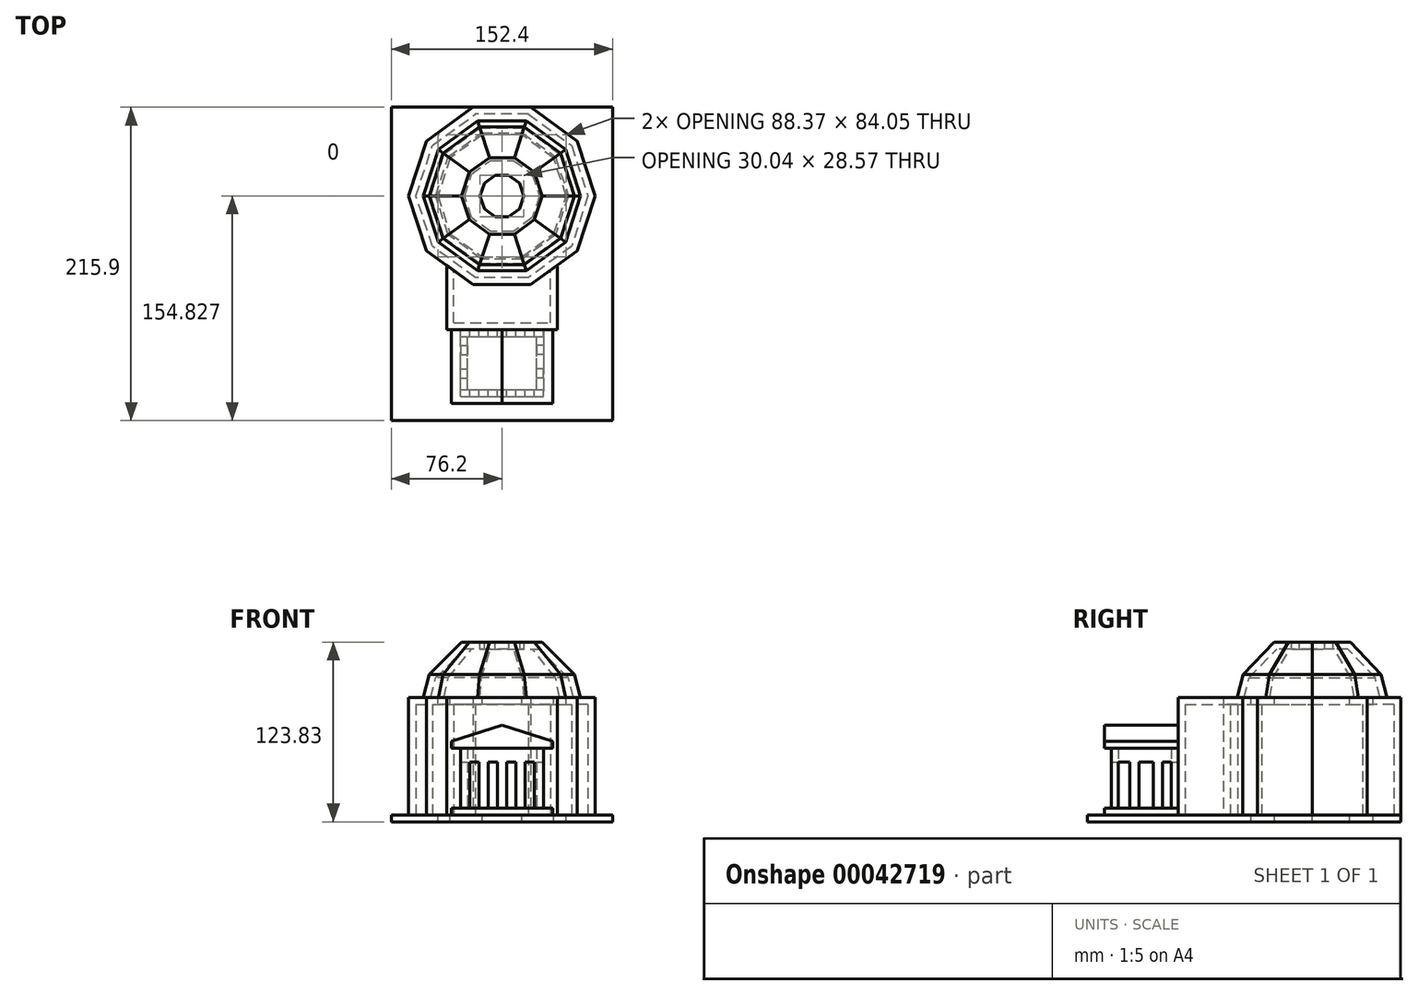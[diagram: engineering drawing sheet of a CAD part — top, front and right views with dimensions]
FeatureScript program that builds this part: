
annotation { "Feature Type Name" : "Feature", "Feature Type Description" : "" }
export const myFeature = defineFeature(function(context is Context, id is Id, definition is map)
    precondition{}
    {
        {
            var Q0;
            Q0=qCreatedBy(makeId("Top.planeOp"),FACE);
            var sketch = newSketch(context, id + "F0", { "sketchPlane" : qUnion([Q0])});
            skLineSegment(sketch, "E0.rect.bottom", {"start": v(76.2, 107.95) * mm, "end": v(-76.2, 107.95) * mm});
            skLineSegment(sketch, "E0.rect.top", {"start": v(76.2, -107.95) * mm, "end": v(-76.2, -107.95) * mm});
            skLineSegment(sketch, "E0.rect.left", {"start": v(76.2, 107.95) * mm, "end": v(76.2, -107.95) * mm});
            skLineSegment(sketch, "E0.rect.right", {"start": v(-76.2, 107.95) * mm, "end": v(-76.2, -107.95) * mm});
            skPoint(sketch, "E0.rect.middle", {"position": v(0, 0) * mm});
            skSolve(sketch);
        }
        {
            var Q0;
            Q0 = qSketchRegion(id + "F0", true);
            extrude(context, id + "F1", {"entities" : qUnion([Q0]), "depth" : 4.76 * mm});
        }
        {
            var Q0;
            Q0=makeQuery(id+"F1.opExtrude","CAP_FACE",FACE,{"disambiguationData":[OSD([sQuery(id+"F0.wireOp",EDGE,"E0.rect.bottom"),sQuery(id+"F0.wireOp",EDGE,"E0.rect.top"),sQuery(id+"F0.wireOp",EDGE,"E0.rect.left"),sQuery(id+"F0.wireOp",EDGE,"E0.rect.right")])],"isStart":false});
            var sketch = newSketch(context, id + "F2", { "sketchPlane" : qUnion([Q0])});
            skLineSegment(sketch, "E1.bottom", {"start": v(-34.93, -96.19) * mm, "end": v(34.92, -96.19) * mm});
            skLineSegment(sketch, "E1.top", {"start": v(-34.93, -45.39) * mm, "end": v(34.92, -45.39) * mm});
            skLineSegment(sketch, "E1.left", {"start": v(-34.93, -96.19) * mm, "end": v(-34.93, -45.39) * mm});
            skLineSegment(sketch, "E1.right", {"start": v(34.92, -96.19) * mm, "end": v(34.92, -45.39) * mm});
            skSolve(sketch);
        }
        {
            var Q0;
            Q0 = qSketchRegion(id + "F2", true);
            extrude(context, id + "F3", {"entities" : qUnion([Q0]), "depth" : 4.76 * mm});
        }
        {
            var Q0;
            Q0=makeQuery(id+"F3.opExtrude","CAP_FACE",FACE,{"disambiguationData":[OSD([sQuery(id+"F2.wireOp",EDGE,"E1.bottom"),sQuery(id+"F2.wireOp",EDGE,"E1.top"),sQuery(id+"F2.wireOp",EDGE,"E1.left"),sQuery(id+"F2.wireOp",EDGE,"E1.right")])],"isStart":false});
            var sketch = newSketch(context, id + "F4", { "sketchPlane" : qUnion([Q0])});
            skLineSegment(sketch, "E2.bottom", {"start": v(-28.58, -91.43) * mm, "end": v(-22.23, -91.43) * mm});
            skLineSegment(sketch, "E2.top", {"start": v(-28.58, -86.66) * mm, "end": v(-22.22, -86.66) * mm});
            skLineSegment(sketch, "E2.left", {"start": v(-28.58, -91.43) * mm, "end": v(-28.58, -86.66) * mm});
            skLineSegment(sketch, "E2.right", {"start": v(-22.22, -91.43) * mm, "end": v(-22.22, -86.66) * mm});
            skLineSegment(sketch, "E3.1.0.0", {"start": v(-15.88, -86.66) * mm, "end": v(-9.52, -86.66) * mm});
            skLineSegment(sketch, "E3.1.0.1", {"start": v(-15.88, -91.43) * mm, "end": v(-15.88, -86.66) * mm});
            skLineSegment(sketch, "E3.1.0.2", {"start": v(-15.88, -91.43) * mm, "end": v(-9.53, -91.43) * mm});
            skLineSegment(sketch, "E3.1.0.3", {"start": v(-9.52, -91.43) * mm, "end": v(-9.52, -86.66) * mm});
            skLineSegment(sketch, "E3.2.0.0", {"start": v(-3.18, -86.66) * mm, "end": v(3.18, -86.66) * mm});
            skLineSegment(sketch, "E3.2.0.1", {"start": v(-3.17, -91.43) * mm, "end": v(-3.17, -86.66) * mm});
            skLineSegment(sketch, "E3.2.0.2", {"start": v(-3.18, -91.43) * mm, "end": v(3.18, -91.43) * mm});
            skLineSegment(sketch, "E3.2.0.3", {"start": v(3.18, -91.43) * mm, "end": v(3.18, -86.66) * mm});
            skLineSegment(sketch, "E3.3.0.0", {"start": v(9.52, -86.66) * mm, "end": v(15.88, -86.66) * mm});
            skLineSegment(sketch, "E3.3.0.1", {"start": v(9.53, -91.43) * mm, "end": v(9.53, -86.66) * mm});
            skLineSegment(sketch, "E3.3.0.2", {"start": v(9.52, -91.43) * mm, "end": v(15.88, -91.43) * mm});
            skLineSegment(sketch, "E3.3.0.3", {"start": v(15.88, -91.43) * mm, "end": v(15.88, -86.66) * mm});
            skLineSegment(sketch, "E3.direction1", {"start": v(-28.58, -86.66) * mm, "end": v(-15.88, -86.66) * mm, "construction": true});
            skLineSegment(sketch, "E4.0.4.0", {"start": v(22.23, -86.66) * mm, "end": v(28.58, -86.66) * mm});
            skLineSegment(sketch, "E4.3.4.0", {"start": v(22.23, -91.43) * mm, "end": v(22.23, -86.66) * mm});
            skLineSegment(sketch, "E4.6.4.0", {"start": v(22.23, -91.43) * mm, "end": v(28.58, -91.43) * mm});
            skLineSegment(sketch, "E4.9.4.0", {"start": v(28.58, -91.43) * mm, "end": v(28.58, -86.66) * mm});
            skLineSegment(sketch, "E5.bottom", {"start": v(-28.58, -50.15) * mm, "end": v(-22.23, -50.15) * mm});
            skLineSegment(sketch, "E6.3.0.0", {"start": v(9.52, -45.39) * mm, "end": v(15.87, -45.39) * mm});
            skLineSegment(sketch, "E6.3.0.2", {"start": v(9.52, -50.15) * mm, "end": v(15.87, -50.15) * mm});
            skLineSegment(sketch, "E7.6.4.0", {"start": v(22.22, -50.15) * mm, "end": v(28.57, -50.15) * mm});
            skLineSegment(sketch, "E5.top", {"start": v(-28.58, -45.39) * mm, "end": v(-22.23, -45.39) * mm});
            skLineSegment(sketch, "E6.3.0.1", {"start": v(9.52, -50.15) * mm, "end": v(9.52, -45.39) * mm});
            skLineSegment(sketch, "E5.left", {"start": v(-28.58, -50.15) * mm, "end": v(-28.58, -45.39) * mm});
            skLineSegment(sketch, "E5.right", {"start": v(-22.23, -50.15) * mm, "end": v(-22.23, -45.39) * mm});
            skLineSegment(sketch, "E6.1.0.0", {"start": v(-15.88, -45.39) * mm, "end": v(-9.53, -45.39) * mm});
            skLineSegment(sketch, "E6.3.0.3", {"start": v(15.87, -50.15) * mm, "end": v(15.87, -45.39) * mm});
            skLineSegment(sketch, "E6.direction1", {"start": v(-28.58, -45.39) * mm, "end": v(-15.88, -45.39) * mm, "construction": true});
            skLineSegment(sketch, "E7.9.4.0", {"start": v(28.57, -50.15) * mm, "end": v(28.57, -45.39) * mm});
            skLineSegment(sketch, "E7.3.4.0", {"start": v(22.22, -50.15) * mm, "end": v(22.22, -45.39) * mm});
            skLineSegment(sketch, "E6.2.0.3", {"start": v(3.17, -50.15) * mm, "end": v(3.17, -45.39) * mm});
            skLineSegment(sketch, "E6.2.0.2", {"start": v(-3.18, -50.15) * mm, "end": v(3.17, -50.15) * mm});
            skLineSegment(sketch, "E7.0.4.0", {"start": v(22.22, -45.39) * mm, "end": v(28.57, -45.39) * mm});
            skLineSegment(sketch, "E6.2.0.1", {"start": v(-3.18, -50.15) * mm, "end": v(-3.18, -45.39) * mm});
            skLineSegment(sketch, "E6.2.0.0", {"start": v(-3.18, -45.39) * mm, "end": v(3.17, -45.39) * mm});
            skLineSegment(sketch, "E6.1.0.3", {"start": v(-9.53, -50.15) * mm, "end": v(-9.53, -45.39) * mm});
            skLineSegment(sketch, "E6.1.0.2", {"start": v(-15.88, -50.15) * mm, "end": v(-9.53, -50.15) * mm});
            skLineSegment(sketch, "E6.1.0.1", {"start": v(-15.88, -50.15) * mm, "end": v(-15.88, -45.39) * mm});
            skLineSegment(sketch, "E8", {"start": v(28.58, -67.47) * mm, "end": v(-34.93, -67.47) * mm, "construction": true});
            skLineSegment(sketch, "E9.bottom", {"start": v(28.57, -78.73) * mm, "end": v(23.81, -78.73) * mm});
            skLineSegment(sketch, "E9.top", {"start": v(28.58, -72.38) * mm, "end": v(23.81, -72.38) * mm});
            skLineSegment(sketch, "E9.left", {"start": v(28.58, -78.73) * mm, "end": v(28.58, -72.38) * mm});
            skLineSegment(sketch, "E9.right", {"start": v(23.81, -78.73) * mm, "end": v(23.81, -72.38) * mm});
            skLineSegment(sketch, "E10.MirrorCS", {"start": v(28.58, -62.56) * mm, "end": v(23.81, -62.56) * mm});
            skLineSegment(sketch, "E11.MirrorCS", {"start": v(23.81, -56.21) * mm, "end": v(23.81, -62.56) * mm});
            skLineSegment(sketch, "E12.MirrorCS", {"start": v(28.58, -56.21) * mm, "end": v(28.58, -62.56) * mm});
            skLineSegment(sketch, "E13.MirrorCS", {"start": v(28.57, -56.21) * mm, "end": v(23.81, -56.21) * mm});
            skLineSegment(sketch, "E14", {"start": v(0, -96.19) * mm, "end": v(0, -45.39) * mm, "construction": true});
            skLineSegment(sketch, "E15.MirrorCS", {"start": v(-28.58, -56.21) * mm, "end": v(-23.81, -56.21) * mm});
            skLineSegment(sketch, "E16.MirrorCS", {"start": v(-28.58, -56.21) * mm, "end": v(-28.58, -62.56) * mm});
            skLineSegment(sketch, "E17.MirrorCS", {"start": v(-28.58, -72.38) * mm, "end": v(-23.81, -72.38) * mm});
            skLineSegment(sketch, "E18.MirrorCS", {"start": v(-28.58, -62.56) * mm, "end": v(-23.81, -62.56) * mm});
            skLineSegment(sketch, "E19.MirrorCS", {"start": v(-28.58, -78.73) * mm, "end": v(-23.81, -78.73) * mm});
            skLineSegment(sketch, "E20.MirrorCS", {"start": v(-23.81, -56.21) * mm, "end": v(-23.81, -62.56) * mm});
            skLineSegment(sketch, "E21.MirrorCS", {"start": v(-28.58, -78.73) * mm, "end": v(-28.58, -72.38) * mm});
            skLineSegment(sketch, "E22.MirrorCS", {"start": v(-23.81, -78.73) * mm, "end": v(-23.81, -72.38) * mm});
            skSolve(sketch);
        }
        {
            var Q0;
            Q0=makeQuery(id+"F4.imprint","IMPRINT",FACE,{"disambiguationData":[TD([[makeQuery(id+"F4.imprint","IMPRINT",EDGE,{"derivedFrom":sQuery(id+"F4.wireOp",EDGE,"E5.bottom")}),1.0]])]});
            var Q1;
            Q1=makeQuery(id+"F4.imprint","IMPRINT",FACE,{"disambiguationData":[TD([[makeQuery(id+"F4.imprint","IMPRINT",EDGE,{"derivedFrom":sQuery(id+"F4.wireOp",EDGE,"E6.1.0.0")}),-1.0]])]});
            var Q2;
            Q2=makeQuery(id+"F4.imprint","IMPRINT",FACE,{"disambiguationData":[TD([[makeQuery(id+"F4.imprint","IMPRINT",EDGE,{"derivedFrom":sQuery(id+"F4.wireOp",EDGE,"E6.2.0.3")}),1.0]])]});
            var Q3;
            Q3=makeQuery(id+"F4.imprint","IMPRINT",FACE,{"disambiguationData":[TD([[makeQuery(id+"F4.imprint","IMPRINT",EDGE,{"derivedFrom":sQuery(id+"F4.wireOp",EDGE,"E6.3.0.0")}),-1.0]])]});
            var Q4;
            Q4=makeQuery(id+"F4.imprint","IMPRINT",FACE,{"disambiguationData":[TD([[makeQuery(id+"F4.imprint","IMPRINT",EDGE,{"derivedFrom":sQuery(id+"F4.wireOp",EDGE,"E7.6.4.0")}),1.0]])]});
            var Q5;
            Q5=makeQuery(id+"F4.imprint","IMPRINT",FACE,{"disambiguationData":[TD([[makeQuery(id+"F4.imprint","IMPRINT",EDGE,{"derivedFrom":sQuery(id+"F4.wireOp",EDGE,"E10.MirrorCS")}),-1.0]])]});
            var Q6;
            Q6=makeQuery(id+"F4.imprint","IMPRINT",FACE,{"disambiguationData":[TD([[makeQuery(id+"F4.imprint","IMPRINT",EDGE,{"derivedFrom":sQuery(id+"F4.wireOp",EDGE,"E9.bottom")}),-1.0]])]});
            var Q7;
            Q7=makeQuery(id+"F4.imprint","IMPRINT",FACE,{"disambiguationData":[TD([[makeQuery(id+"F4.imprint","IMPRINT",EDGE,{"derivedFrom":sQuery(id+"F4.wireOp",EDGE,"E4.0.4.0")}),-1.0]])]});
            var Q8;
            Q8=makeQuery(id+"F4.imprint","IMPRINT",FACE,{"disambiguationData":[TD([[makeQuery(id+"F4.imprint","IMPRINT",EDGE,{"derivedFrom":sQuery(id+"F4.wireOp",EDGE,"E3.3.0.0")}),-1.0]])]});
            var Q9;
            Q9=makeQuery(id+"F4.imprint","IMPRINT",FACE,{"disambiguationData":[TD([[makeQuery(id+"F4.imprint","IMPRINT",EDGE,{"derivedFrom":sQuery(id+"F4.wireOp",EDGE,"E3.2.0.0")}),-1.0]])]});
            var Q10;
            Q10=makeQuery(id+"F4.imprint","IMPRINT",FACE,{"disambiguationData":[TD([[makeQuery(id+"F4.imprint","IMPRINT",EDGE,{"derivedFrom":sQuery(id+"F4.wireOp",EDGE,"E3.1.0.0")}),-1.0]])]});
            var Q11;
            Q11=makeQuery(id+"F4.imprint","IMPRINT",FACE,{"disambiguationData":[TD([[makeQuery(id+"F4.imprint","IMPRINT",EDGE,{"derivedFrom":sQuery(id+"F4.wireOp",EDGE,"E2.bottom")}),1.0]])]});
            var Q12;
            Q12=makeQuery(id+"F4.imprint","IMPRINT",FACE,{"disambiguationData":[TD([[makeQuery(id+"F4.imprint","IMPRINT",EDGE,{"derivedFrom":sQuery(id+"F4.wireOp",EDGE,"E17.MirrorCS")}),-1.0]])]});
            var Q13;
            Q13=makeQuery(id+"F4.imprint","IMPRINT",FACE,{"disambiguationData":[TD([[makeQuery(id+"F4.imprint","IMPRINT",EDGE,{"derivedFrom":sQuery(id+"F4.wireOp",EDGE,"E15.MirrorCS")}),-1.0]])]});
            extrude(context, id + "F5", {"entities" : qUnion([Q0, Q1, Q2, Q3, Q4, Q5, Q6, Q7, Q8, Q9, Q10, Q11, Q12, Q13]), "operationType" : NewBodyOperationType.ADD, "depth" : 31.75 * mm});
        }
        {
            var Q0;
            Q0=makeQuery(id+"F5.opExtrude","CAP_FACE",FACE,{"disambiguationData":[OSD([sQuery(id+"F4.wireOp",EDGE,"E5.bottom"),sQuery(id+"F4.wireOp",EDGE,"E5.top"),sQuery(id+"F4.wireOp",EDGE,"E5.left"),sQuery(id+"F4.wireOp",EDGE,"E5.right")])],"isStart":false});
            var sketch = newSketch(context, id + "F6", { "sketchPlane" : qUnion([Q0])});
            skPoint(sketch, "E23.0", {"position": v(-28.58, -45.39) * mm});
            skPoint(sketch, "E24.0", {"position": v(-23.81, -56.21) * mm});
            skPoint(sketch, "E25.0", {"position": v(28.58, -91.43) * mm});
            skPoint(sketch, "E26.0", {"position": v(23.81, -78.73) * mm});
            skLineSegment(sketch, "E27.bottom", {"start": v(-28.58, -45.39) * mm, "end": v(28.58, -45.39) * mm});
            skLineSegment(sketch, "E27.top", {"start": v(-28.58, -91.43) * mm, "end": v(28.58, -91.43) * mm});
            skLineSegment(sketch, "E27.left", {"start": v(-28.58, -45.39) * mm, "end": v(-28.58, -91.43) * mm});
            skLineSegment(sketch, "E27.right", {"start": v(28.57, -45.39) * mm, "end": v(28.57, -91.43) * mm});
            skLineSegment(sketch, "E28.0", {"start": v(22.23, -86.66) * mm, "end": v(28.58, -86.66) * mm});
            skLineSegment(sketch, "E29.0", {"start": v(-28.58, -50.15) * mm, "end": v(-22.23, -50.15) * mm});
            skPoint(sketch, "E30.firstSnap0", {"position": v(25.4, -86.66) * mm});
            skLineSegment(sketch, "E30.bottom", {"start": v(23.81, -86.66) * mm, "end": v(-23.81, -86.66) * mm});
            skLineSegment(sketch, "E30.top", {"start": v(23.81, -50.15) * mm, "end": v(-23.81, -50.15) * mm});
            skLineSegment(sketch, "E30.left", {"start": v(23.81, -86.66) * mm, "end": v(23.81, -50.15) * mm});
            skLineSegment(sketch, "E30.right", {"start": v(-23.81, -86.66) * mm, "end": v(-23.81, -50.15) * mm});
            skSolve(sketch);
        }
        {
            var Q0;
            Q0 = qSketchRegion(id + "F6", true);
            extrude(context, id + "F7", {"entities" : qUnion([Q0]), "operationType" : NewBodyOperationType.ADD, "depth" : 9.52 * mm});
        }
        {
            var Q0;
            Q0=makeQuery(id+"F3.opExtrude","SWEPT_FACE",FACE,{"disambiguationData":[OSD([sQuery(id+"F2.wireOp",EDGE,"E1.bottom")])]});
            var sketch = newSketch(context, id + "F8", { "sketchPlane" : qUnion([Q0])});
            skLineSegment(sketch, "E31.0", {"start": v(-28.58, 50.8) * mm, "end": v(28.58, 50.8) * mm});
            skLineSegment(sketch, "E32", {"start": v(-34.93, 50.8) * mm, "end": v(-28.58, 50.8) * mm});
            skLineSegment(sketch, "E33", {"start": v(34.92, 50.8) * mm, "end": v(28.58, 50.8) * mm});
            skLineSegment(sketch, "E34", {"start": v(34.92, 50.8) * mm, "end": v(34.92, 55.56) * mm});
            skLineSegment(sketch, "E35", {"start": v(-34.93, 50.8) * mm, "end": v(-34.93, 55.56) * mm});
            skLineSegment(sketch, "E36", {"start": v(0, 50.8) * mm, "end": v(0, 66.67) * mm, "construction": true});
            skPoint(sketch, "E36.endSnap0", {"position": v(0, 50.8) * mm});
            skLineSegment(sketch, "E37", {"start": v(0, 66.67) * mm, "end": v(-34.93, 55.56) * mm});
            skLineSegment(sketch, "E38", {"start": v(0, 66.67) * mm, "end": v(34.92, 55.56) * mm});
            skSolve(sketch);
        }
        {
            var Q0;
            Q0 = qSketchRegion(id + "F8", true);
            var Q1;
            Q1=makeQuery(id+"F7.boolean.opBoolean","MERGE",FACE,{"derivedFrom":[makeQuery(id+"F5.boolean.opBoolean","MERGE",FACE,{"derivedFrom":[makeQuery(id+"F3.opExtrude","SWEPT_FACE",FACE,{"disambiguationData":[OSD([sQuery(id+"F2.wireOp",EDGE,"E1.top")])]}),makeQuery(id+"F5.opExtrude","SWEPT_FACE",FACE,{"disambiguationData":[OSD([sQuery(id+"F4.wireOp",EDGE,"E6.3.0.0")])]}),makeQuery(id+"F5.opExtrude","SWEPT_FACE",FACE,{"disambiguationData":[OSD([sQuery(id+"F4.wireOp",EDGE,"E5.top")])]}),makeQuery(id+"F5.opExtrude","SWEPT_FACE",FACE,{"disambiguationData":[OSD([sQuery(id+"F4.wireOp",EDGE,"E6.1.0.0")])]}),makeQuery(id+"F5.opExtrude","SWEPT_FACE",FACE,{"disambiguationData":[OSD([sQuery(id+"F4.wireOp",EDGE,"E7.0.4.0")])]}),makeQuery(id+"F5.opExtrude","SWEPT_FACE",FACE,{"disambiguationData":[OSD([sQuery(id+"F4.wireOp",EDGE,"E6.2.0.0")])]})]}),makeQuery(id+"F7.opExtrude","SWEPT_FACE",FACE,{"disambiguationData":[OSD([sQuery(id+"F6.wireOp",EDGE,"E27.bottom")])]})]});
            extrude(context, id + "F9", {"entities" : qUnion([Q0]), "operationType" : NewBodyOperationType.ADD, "endBound" : BoundingType.UP_TO_SURFACE, "oppositeDirection" : true, "endBoundEntityFace" : qUnion([Q1]), "depth" : 25.4 * mm});
        }
        {
            var Q0;
            Q0=makeQuery(id+"F1.opExtrude","CAP_FACE",FACE,{"disambiguationData":[OSD([sQuery(id+"F0.wireOp",EDGE,"E0.rect.bottom"),sQuery(id+"F0.wireOp",EDGE,"E0.rect.top"),sQuery(id+"F0.wireOp",EDGE,"E0.rect.left"),sQuery(id+"F0.wireOp",EDGE,"E0.rect.right")])],"isStart":false});
            var sketch = newSketch(context, id + "F10", { "sketchPlane" : qUnion([Q0])});
            skCircle(sketch, "E39.cCircle", {"center": v(0, 46.88) * mm, "radius": 61.07 * mm, "construction": true});
            skLineSegment(sketch, "E39.0", {"start": v(-19.84, 107.95) * mm, "end": v(19.84, 107.95) * mm});
            skLineSegment(sketch, "E39.1", {"start": v(19.84, 107.95) * mm, "end": v(51.95, 84.62) * mm});
            skLineSegment(sketch, "E39.2", {"start": v(51.95, 84.62) * mm, "end": v(64.22, 46.88) * mm});
            skLineSegment(sketch, "E39.3", {"start": v(64.22, 46.88) * mm, "end": v(51.95, 9.13) * mm});
            skLineSegment(sketch, "E39.4", {"start": v(51.95, 9.13) * mm, "end": v(19.84, -14.2) * mm});
            skLineSegment(sketch, "E39.5", {"start": v(19.84, -14.2) * mm, "end": v(-19.84, -14.2) * mm});
            skLineSegment(sketch, "E39.6", {"start": v(-19.84, -14.2) * mm, "end": v(-51.95, 9.13) * mm});
            skLineSegment(sketch, "E39.7", {"start": v(-51.95, 9.13) * mm, "end": v(-64.22, 46.88) * mm});
            skLineSegment(sketch, "E39.8", {"start": v(-64.22, 46.88) * mm, "end": v(-51.95, 84.62) * mm});
            skLineSegment(sketch, "E39.9", {"start": v(-51.95, 84.62) * mm, "end": v(-19.84, 107.95) * mm});
            skPoint(sketch, "E39.0.midPoint", {"position": v(0, 107.95) * mm});
            skSolve(sketch);
        }
        {
            var Q0;
            Q0 = qSketchRegion(id + "F10", true);
            extrude(context, id + "F11", {"entities" : qUnion([Q0]), "depth" : 80.96 * mm});
        }
        {
            var Q0;
            Q0=makeQuery(id+"F1.opExtrude","CAP_FACE",FACE,{"disambiguationData":[OSD([sQuery(id+"F0.wireOp",EDGE,"E0.rect.bottom"),sQuery(id+"F0.wireOp",EDGE,"E0.rect.top"),sQuery(id+"F0.wireOp",EDGE,"E0.rect.left"),sQuery(id+"F0.wireOp",EDGE,"E0.rect.right")])],"isStart":false});
            var sketch = newSketch(context, id + "F12", { "sketchPlane" : qUnion([Q0])});
            skLineSegment(sketch, "E40.0", {"start": v(-19.84, -14.2) * mm, "end": v(-51.95, 9.13) * mm});
            skLineSegment(sketch, "E41.0", {"start": v(19.84, -14.2) * mm, "end": v(-19.84, -14.2) * mm});
            skLineSegment(sketch, "E42.0", {"start": v(51.95, 9.13) * mm, "end": v(19.84, -14.2) * mm});
            skLineSegment(sketch, "E43.0", {"start": v(-34.93, -44.45) * mm, "end": v(34.92, -44.45) * mm});
            skLineSegment(sketch, "E44", {"start": v(-38.1, -45.39) * mm, "end": v(38.1, -45.39) * mm});
            skPoint(sketch, "E45.0", {"position": v(0, -45.39) * mm});
            skLineSegment(sketch, "E46", {"start": v(-38.1, -45.39) * mm, "end": v(-38.1, -0.93) * mm});
            skLineSegment(sketch, "E47", {"start": v(38.1, -45.39) * mm, "end": v(38.1, -0.93) * mm});
            skSolve(sketch);
        }
        {
            var Q0;
            Q0 = qSketchRegion(id + "F12", true);
            extrude(context, id + "F13", {"entities" : qUnion([Q0]), "depth" : 80.96 * mm});
        }
        {
            var Q0;
            Q0=makeQuery(id+"F11.opExtrude","CAP_FACE",FACE,{"disambiguationData":[OSD([sQuery(id+"F10.wireOp",EDGE,"E39.0"),sQuery(id+"F10.wireOp",EDGE,"E39.1"),sQuery(id+"F10.wireOp",EDGE,"E39.2"),sQuery(id+"F10.wireOp",EDGE,"E39.3"),sQuery(id+"F10.wireOp",EDGE,"E39.4"),sQuery(id+"F10.wireOp",EDGE,"E39.5"),sQuery(id+"F10.wireOp",EDGE,"E39.6"),sQuery(id+"F10.wireOp",EDGE,"E39.7"),sQuery(id+"F10.wireOp",EDGE,"E39.8"),sQuery(id+"F10.wireOp",EDGE,"E39.9")])],"isStart":true});
            shell(context, id + "F14", {"entities" : qUnion([Q0]), "thickness" : 4.76 * mm});
        }
        {
            var Q0;
            Q0=makeQuery(id+"F13.opExtrude","CAP_FACE",FACE,{"disambiguationData":[OSD([sQuery(id+"F12.wireOp",EDGE,"E40.0"),sQuery(id+"F12.wireOp",EDGE,"E41.0"),sQuery(id+"F12.wireOp",EDGE,"E42.0"),sQuery(id+"F12.wireOp",EDGE,"E44"),sQuery(id+"F12.wireOp",EDGE,"E46"),sQuery(id+"F12.wireOp",EDGE,"E47")])],"isStart":true});
            var Q1;
            Q1=makeQuery(id+"F13.opExtrude","SWEPT_FACE",FACE,{"disambiguationData":[OSD([sQuery(id+"F12.wireOp",EDGE,"E41.0")])]});
            var Q2;
            Q2=makeQuery(id+"F13.opExtrude","SWEPT_FACE",FACE,{"disambiguationData":[OSD([sQuery(id+"F12.wireOp",EDGE,"E42.0")])]});
            var Q3;
            Q3=makeQuery(id+"F13.opExtrude","SWEPT_FACE",FACE,{"disambiguationData":[OSD([sQuery(id+"F12.wireOp",EDGE,"E40.0")])]});
            shell(context, id + "F15", {"entities" : qUnion([Q0, Q1, Q2, Q3]), "thickness" : 4.76 * mm});
        }
        {
            var Q0;
            Q0=makeQuery(id+"F11.opExtrude","CAP_FACE",FACE,{"disambiguationData":[OSD([sQuery(id+"F10.wireOp",EDGE,"E39.0"),sQuery(id+"F10.wireOp",EDGE,"E39.1"),sQuery(id+"F10.wireOp",EDGE,"E39.2"),sQuery(id+"F10.wireOp",EDGE,"E39.3"),sQuery(id+"F10.wireOp",EDGE,"E39.4"),sQuery(id+"F10.wireOp",EDGE,"E39.5"),sQuery(id+"F10.wireOp",EDGE,"E39.6"),sQuery(id+"F10.wireOp",EDGE,"E39.7"),sQuery(id+"F10.wireOp",EDGE,"E39.8"),sQuery(id+"F10.wireOp",EDGE,"E39.9")])],"isStart":false});
            var sketch = newSketch(context, id + "F16", { "sketchPlane" : qUnion([Q0])});
            skLineSegment(sketch, "E48.0", {"start": v(44.19, 46.88) * mm, "end": v(35.75, 72.85) * mm});
            skLineSegment(sketch, "E48.1", {"start": v(35.75, 20.9) * mm, "end": v(44.19, 46.88) * mm});
            skLineSegment(sketch, "E48.2", {"start": v(35.75, 72.85) * mm, "end": v(13.65, 88.9) * mm});
            skLineSegment(sketch, "E48.3", {"start": v(13.65, 4.85) * mm, "end": v(35.75, 20.9) * mm});
            skLineSegment(sketch, "E48.4", {"start": v(-13.65, 4.85) * mm, "end": v(13.65, 4.85) * mm});
            skLineSegment(sketch, "E48.5", {"start": v(-35.75, 20.9) * mm, "end": v(-13.65, 4.85) * mm});
            skLineSegment(sketch, "E48.6", {"start": v(13.65, 88.9) * mm, "end": v(-13.65, 88.9) * mm});
            skLineSegment(sketch, "E48.7", {"start": v(-13.65, 88.9) * mm, "end": v(-35.75, 72.85) * mm});
            skLineSegment(sketch, "E48.8", {"start": v(-35.75, 72.85) * mm, "end": v(-44.19, 46.88) * mm});
            skLineSegment(sketch, "E48.9", {"start": v(-44.19, 46.88) * mm, "end": v(-35.75, 20.9) * mm});
            skSolve(sketch);
        }
        {
            var Q0;
            Q0=makeQuery(id+"F16.imprint","IMPRINT",FACE,{"disambiguationData":[TD([[makeQuery(id+"F16.imprint","IMPRINT",EDGE,{"derivedFrom":sQuery(id+"F16.wireOp",EDGE,"E48.0")}),1.0]])]});
            extrude(context, id + "F17", {"entities" : qUnion([Q0]), "operationType" : NewBodyOperationType.REMOVE, "endBound" : BoundingType.THROUGH_ALL, "oppositeDirection" : true, "depth" : 25.4 * mm});
        }
        {
            var Q0;
            Q0=makeQuery(id+"F11.opExtrude","CAP_FACE",FACE,{"disambiguationData":[OSD([sQuery(id+"F10.wireOp",EDGE,"E39.0"),sQuery(id+"F10.wireOp",EDGE,"E39.1"),sQuery(id+"F10.wireOp",EDGE,"E39.2"),sQuery(id+"F10.wireOp",EDGE,"E39.3"),sQuery(id+"F10.wireOp",EDGE,"E39.4"),sQuery(id+"F10.wireOp",EDGE,"E39.5"),sQuery(id+"F10.wireOp",EDGE,"E39.6"),sQuery(id+"F10.wireOp",EDGE,"E39.7"),sQuery(id+"F10.wireOp",EDGE,"E39.8"),sQuery(id+"F10.wireOp",EDGE,"E39.9")])],"isStart":false});
            var sketch = newSketch(context, id + "F18", { "sketchPlane" : qUnion([Q0])});
            skLineSegment(sketch, "E49.0", {"start": v(54.2, 46.88) * mm, "end": v(43.85, 78.74) * mm});
            skLineSegment(sketch, "E49.1", {"start": v(43.85, 15.02) * mm, "end": v(54.2, 46.88) * mm});
            skLineSegment(sketch, "E49.2", {"start": v(43.85, 78.74) * mm, "end": v(16.75, 98.43) * mm});
            skLineSegment(sketch, "E49.3", {"start": v(16.75, -4.67) * mm, "end": v(43.85, 15.02) * mm});
            skLineSegment(sketch, "E49.4", {"start": v(-16.75, -4.67) * mm, "end": v(16.75, -4.67) * mm});
            skLineSegment(sketch, "E49.5", {"start": v(-43.85, 15.02) * mm, "end": v(-16.75, -4.67) * mm});
            skLineSegment(sketch, "E49.6", {"start": v(16.75, 98.43) * mm, "end": v(-16.75, 98.43) * mm});
            skLineSegment(sketch, "E49.7", {"start": v(-16.75, 98.43) * mm, "end": v(-43.85, 78.74) * mm});
            skLineSegment(sketch, "E49.8", {"start": v(-43.85, 78.74) * mm, "end": v(-54.2, 46.88) * mm});
            skLineSegment(sketch, "E49.9", {"start": v(-54.2, 46.88) * mm, "end": v(-43.85, 15.02) * mm});
            skSolve(sketch);
        }
        {
            var Q0;
            Q0=makeQuery(id+"F11.opExtrude","SWEPT_FACE",FACE,{"disambiguationData":[OSD([sQuery(id+"F10.wireOp",EDGE,"E39.7")])]});
            var Q1;
            Q1=makeQuery(id+"F11.opExtrude","SWEPT_FACE",FACE,{"disambiguationData":[OSD([sQuery(id+"F10.wireOp",EDGE,"E39.2")])]});
            cPlane(context, id + "F19", {"entities" : qUnion([Q0, Q1]), "cplaneType" : CPlaneType.MID_PLANE, "offset" : 152.4 * mm, "width" : 152.4 * mm, "height" : 152.4 * mm});
        }
        {
            var Q0;
            Q0=qCreatedBy(id+"F19.planeOp",FACE);
            var sketch = newSketch(context, id + "F20", { "sketchPlane" : qUnion([Q0])});
            skPoint(sketch, "E50.0", {"position": v(9.62, 85.73) * mm});
            skLineSegment(sketch, "E51.0.0", {"start": v(-0.73, 85.73) * mm, "end": v(-27.83, 85.73) * mm});
            skLineSegment(sketch, "E51.0.1", {"start": v(-27.83, 85.73) * mm, "end": v(-61.33, 85.73) * mm});
            skLineSegment(sketch, "E51.0.2", {"start": v(-61.33, 85.73) * mm, "end": v(-88.43, 85.73) * mm});
            skLineSegment(sketch, "E51.0.3", {"start": v(-88.43, 85.73) * mm, "end": v(-98.78, 85.73) * mm});
            skLineSegment(sketch, "E51.0.4", {"start": v(-98.78, 85.73) * mm, "end": v(-88.43, 85.73) * mm});
            skLineSegment(sketch, "E51.0.5", {"start": v(-88.43, 85.73) * mm, "end": v(-61.33, 85.73) * mm});
            skLineSegment(sketch, "E51.0.6", {"start": v(-61.33, 85.73) * mm, "end": v(-27.83, 85.73) * mm});
            skLineSegment(sketch, "E51.0.7", {"start": v(-27.83, 85.73) * mm, "end": v(-0.73, 85.73) * mm});
            skLineSegment(sketch, "E51.0.8", {"start": v(-0.73, 85.73) * mm, "end": v(9.62, 85.73) * mm});
            skLineSegment(sketch, "E51.0.9", {"start": v(9.62, 85.73) * mm, "end": v(-0.73, 85.73) * mm});
            skLineSegment(sketch, "E52", {"start": v(-44.58, 85.73) * mm, "end": v(-44.58, 123.83) * mm});
            skLineSegment(sketch, "E53", {"start": v(9.62, 85.73) * mm, "end": v(5.36, 101.6) * mm});
            skPoint(sketch, "E53.endSnap0", {"position": v(4.44, 85.73) * mm});
            skLineSegment(sketch, "E54", {"start": v(5.36, 101.6) * mm, "end": v(-16.86, 123.83) * mm});
            skLineSegment(sketch, "E55", {"start": v(-16.86, 123.83) * mm, "end": v(-44.58, 123.83) * mm});
            skLineSegment(sketch, "E56.0", {"start": v(-18.83, 119.06) * mm, "end": v(-44.58, 119.06) * mm});
            skLineSegment(sketch, "E56.1", {"start": v(1.1, 99.13) * mm, "end": v(-18.83, 119.06) * mm});
            skLineSegment(sketch, "E56.2", {"start": v(5.22, 83.72) * mm, "end": v(1.1, 99.13) * mm});
            skLineSegment(sketch, "E57", {"start": v(-29.56, 123.83) * mm, "end": v(-29.56, 119.06) * mm});
            skSolve(sketch);
        }
        {
            var Q0;
            {var subQ7=sQuery(id+"F20.wireOp",EDGE,"E53");Q0=makeQuery(id+"F20.imprint","IMPRINT",FACE,{"disambiguationData":[TD([[makeQuery(id+"F20.imprint","IMPRINT",EDGE,{"derivedFrom":subQ7}),1.0]])]});}
            var Q1;
            Q1=sQuery(id+"F18.wireOp",EDGE,"E49.3");
            var Q2;
            Q2=sQuery(id+"F18.wireOp",EDGE,"E49.1");
            var Q3;
            Q3=sQuery(id+"F18.wireOp",EDGE,"E49.0");
            var Q4;
            Q4=sQuery(id+"F18.wireOp",EDGE,"E49.2");
            var Q5;
            Q5=sQuery(id+"F18.wireOp",EDGE,"E49.6");
            var Q6;
            Q6=sQuery(id+"F18.wireOp",EDGE,"E49.7");
            var Q7;
            Q7=sQuery(id+"F18.wireOp",EDGE,"E49.8");
            var Q8;
            Q8=sQuery(id+"F18.wireOp",EDGE,"E49.9");
            var Q9;
            Q9=sQuery(id+"F18.wireOp",EDGE,"E49.5");
            var Q10;
            Q10=sQuery(id+"F18.wireOp",EDGE,"E49.4");
            sweep(context, id + "F21", {"profiles" : qUnion([Q0]), "path" : qUnion([Q1, Q2, Q3, Q4, Q5, Q6, Q7, Q8, Q9, Q10])});
        }
    });
